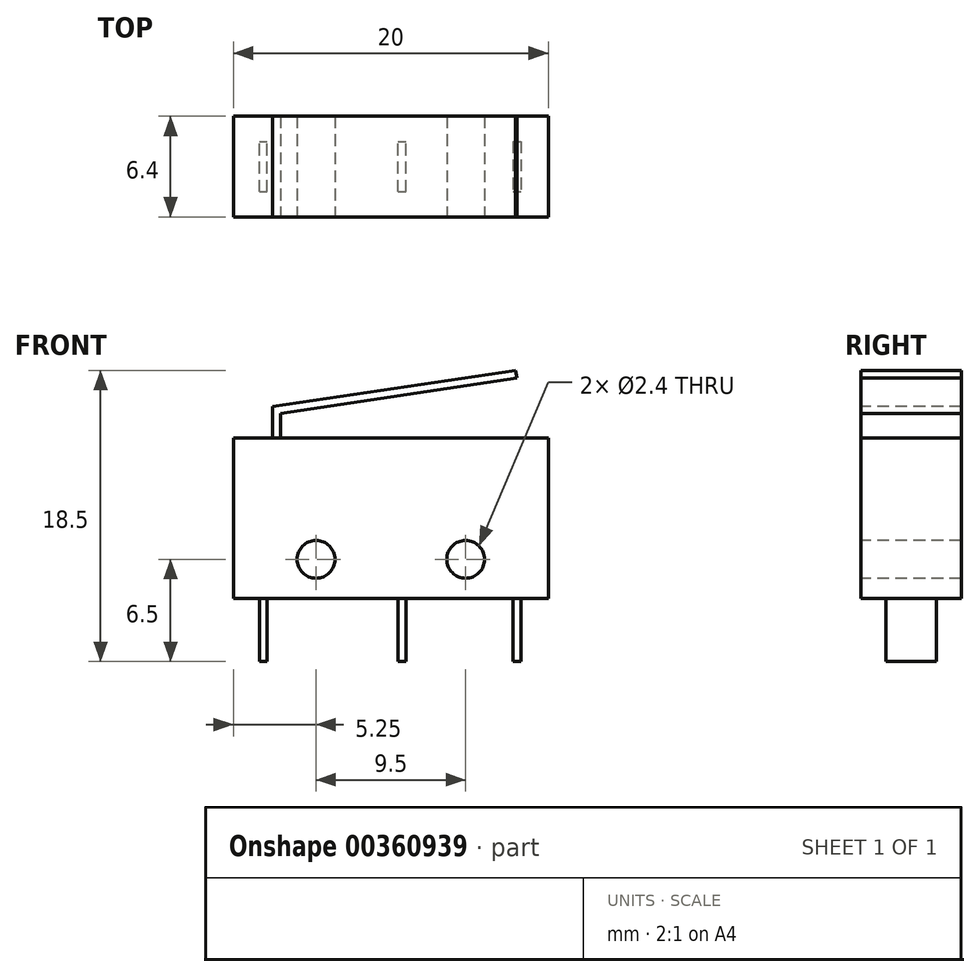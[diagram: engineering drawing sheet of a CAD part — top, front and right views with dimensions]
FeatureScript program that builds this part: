
annotation { "Feature Type Name" : "Feature", "Feature Type Description" : "" }
export const myFeature = defineFeature(function(context is Context, id is Id, definition is map)
    precondition{}
    {
        {
            var Q0;
            Q0=qCreatedBy(makeId("Front.planeOp"),FACE);
            var sketch = newSketch(context, id + "F0", { "sketchPlane" : qUnion([Q0])});
            skLineSegment(sketch, "E0.bottom", {"start": v(-10, 5.1) * mm, "end": v(10, 5.1) * mm});
            skLineSegment(sketch, "E0.top", {"start": v(-10, -5.1) * mm, "end": v(10, -5.1) * mm});
            skLineSegment(sketch, "E0.left", {"start": v(-10, 5.1) * mm, "end": v(-10, -5.1) * mm});
            skLineSegment(sketch, "E0.right", {"start": v(10, 5.1) * mm, "end": v(10, -5.1) * mm});
            skPoint(sketch, "E0.middle", {"position": v(0, 0) * mm});
            skSolve(sketch);
        }
        {
            var Q0;
            Q0 = qSketchRegion(id + "F0", true);
            extrude(context, id + "F1", {"entities" : qUnion([Q0]), "depth" : 6.4 * mm});
        }
        {
            var Q0;
            Q0=makeQuery(id+"F1.opExtrude","CAP_FACE",FACE,{"disambiguationData":[OSD([sQuery(id+"F0.wireOp",EDGE,"E0.bottom"),sQuery(id+"F0.wireOp",EDGE,"E0.top"),sQuery(id+"F0.wireOp",EDGE,"E0.left"),sQuery(id+"F0.wireOp",EDGE,"E0.right")])],"isStart":false});
            var sketch = newSketch(context, id + "F2", { "sketchPlane" : qUnion([Q0])});
            skCircle(sketch, "E1", {"center": v(-4.75, -2.6) * mm, "radius": 1.2 * mm});
            skCircle(sketch, "E2", {"center": v(4.75, -2.6) * mm, "radius": 1.2 * mm});
            skSolve(sketch);
        }
        {
            var Q0;
            Q0 = qSketchRegion(id + "F2", true);
            extrude(context, id + "F3", {"entities" : qUnion([Q0]), "operationType" : NewBodyOperationType.REMOVE, "oppositeDirection" : true, "depth" : 25 * mm});
        }
        {
            var Q0;
            Q0=makeQuery(id+"F1.opExtrude","CAP_FACE",FACE,{"disambiguationData":[OSD([sQuery(id+"F0.wireOp",EDGE,"E0.bottom"),sQuery(id+"F0.wireOp",EDGE,"E0.top"),sQuery(id+"F0.wireOp",EDGE,"E0.left"),sQuery(id+"F0.wireOp",EDGE,"E0.right")])],"isStart":false});
            var sketch = newSketch(context, id + "F4", { "sketchPlane" : qUnion([Q0])});
            skLineSegment(sketch, "E3", {"start": v(-7.5, 7.1) * mm, "end": v(7.93, 9.4) * mm});
            skLineSegment(sketch, "E4", {"start": v(7.93, 9.4) * mm, "end": v(8, 8.9) * mm});
            skLineSegment(sketch, "E5", {"start": v(8, 8.9) * mm, "end": v(-7, 6.67) * mm});
            skLineSegment(sketch, "E6", {"start": v(-7, 6.67) * mm, "end": v(-7, 5.1) * mm});
            skLineSegment(sketch, "E7", {"start": v(-7, 5.1) * mm, "end": v(-7.5, 5.1) * mm});
            skLineSegment(sketch, "E8", {"start": v(-7.5, 5.1) * mm, "end": v(-7.5, 7.1) * mm});
            skPoint(sketch, "E9", {"position": v(4.75, -2.6) * mm});
            skSolve(sketch);
        }
        {
            var Q0;
            Q0 = qSketchRegion(id + "F4", true);
            extrude(context, id + "F5", {"entities" : qUnion([Q0]), "oppositeDirection" : true, "depth" : 6.4 * mm});
        }
        {
            var Q0;
            Q0=makeQuery(id+"F1.opExtrude","SWEPT_FACE",FACE,{"disambiguationData":[OSD([sQuery(id+"F0.wireOp",EDGE,"E0.top")])]});
            var sketch = newSketch(context, id + "F6", { "sketchPlane" : qUnion([Q0])});
            skLineSegment(sketch, "E10.bottom", {"start": v(-8.35, 4.8) * mm, "end": v(-7.85, 4.8) * mm});
            skLineSegment(sketch, "E10.top", {"start": v(-8.35, 1.6) * mm, "end": v(-7.85, 1.6) * mm});
            skLineSegment(sketch, "E10.left", {"start": v(-8.35, 4.8) * mm, "end": v(-8.35, 1.6) * mm});
            skLineSegment(sketch, "E10.right", {"start": v(-7.85, 4.8) * mm, "end": v(-7.85, 1.6) * mm});
            skLineSegment(sketch, "E11.bottom", {"start": v(0.45, 4.8) * mm, "end": v(0.95, 4.8) * mm});
            skLineSegment(sketch, "E11.top", {"start": v(0.45, 1.6) * mm, "end": v(0.95, 1.6) * mm});
            skLineSegment(sketch, "E11.left", {"start": v(0.45, 4.8) * mm, "end": v(0.45, 1.6) * mm});
            skLineSegment(sketch, "E11.right", {"start": v(0.95, 4.8) * mm, "end": v(0.95, 1.6) * mm});
            skLineSegment(sketch, "E12.bottom", {"start": v(7.75, 1.6) * mm, "end": v(8.25, 1.6) * mm});
            skLineSegment(sketch, "E12.top", {"start": v(7.75, 4.8) * mm, "end": v(8.25, 4.8) * mm});
            skLineSegment(sketch, "E12.left", {"start": v(7.75, 1.6) * mm, "end": v(7.75, 4.8) * mm});
            skLineSegment(sketch, "E12.right", {"start": v(8.25, 1.6) * mm, "end": v(8.25, 4.8) * mm});
            skPoint(sketch, "E13", {"position": v(-8.1, 4.8) * mm});
            skPoint(sketch, "E14", {"position": v(0.7, 4.8) * mm});
            skPoint(sketch, "E15", {"position": v(8, 4.8) * mm});
            skPoint(sketch, "E16", {"position": v(-10, 3.2) * mm});
            skSolve(sketch);
        }
        {
            var Q0;
            Q0 = qSketchRegion(id + "F6", true);
            extrude(context, id + "F7", {"entities" : qUnion([Q0]), "depth" : 4 * mm});
        }
    });
